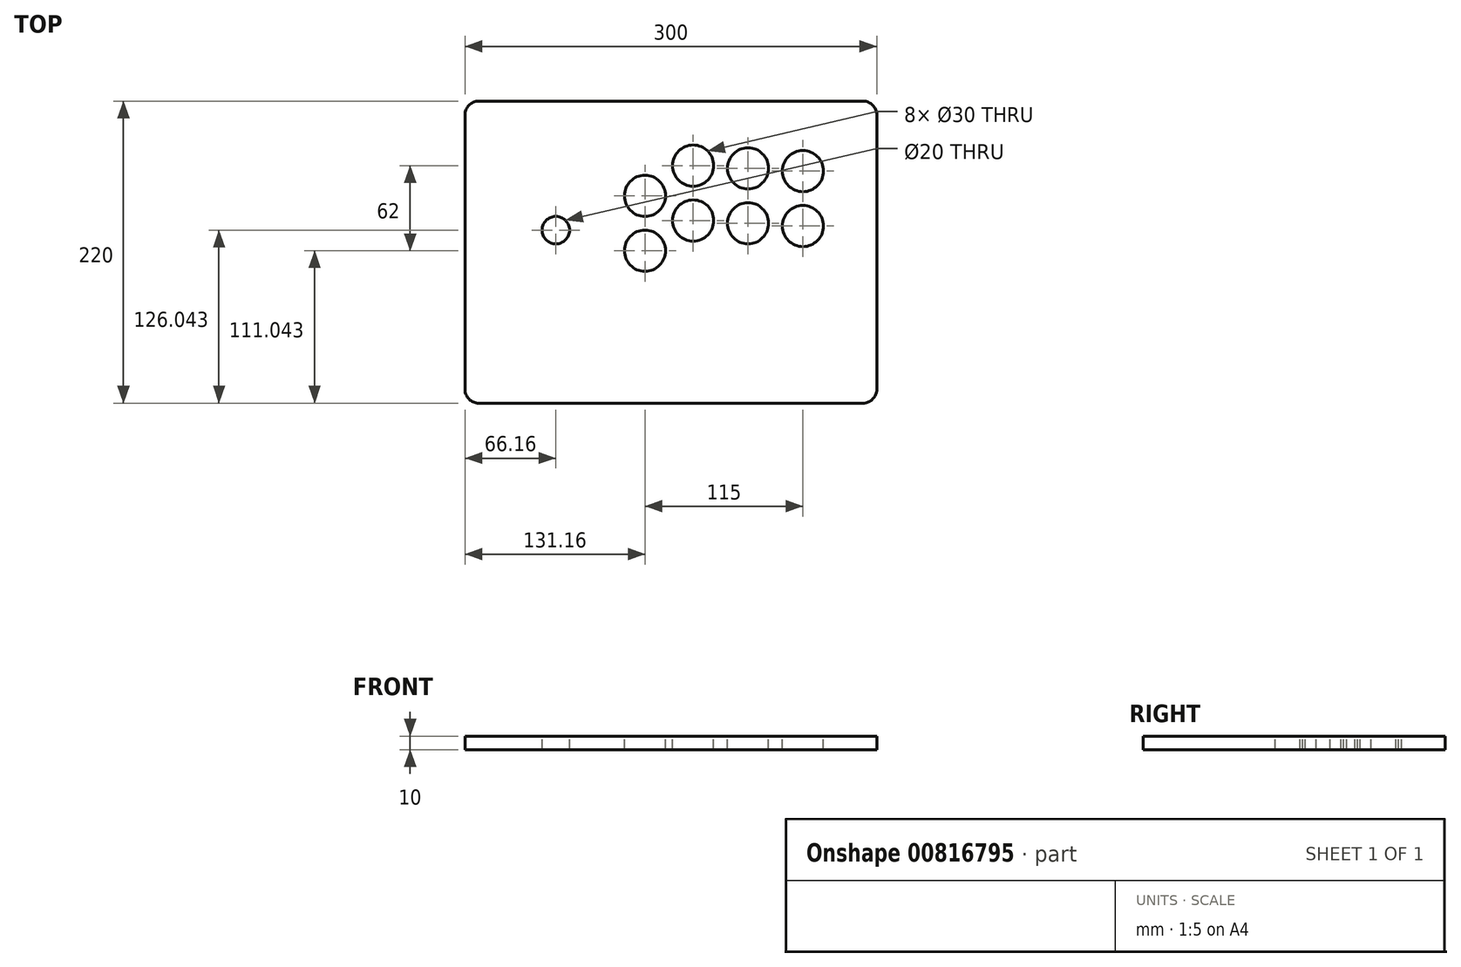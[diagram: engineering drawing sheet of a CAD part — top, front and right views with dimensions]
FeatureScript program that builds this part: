
annotation { "Feature Type Name" : "Feature", "Feature Type Description" : "" }
export const myFeature = defineFeature(function(context is Context, id is Id, definition is map)
    precondition{}
    {
        {
            var Q0;
            Q0=qCreatedBy(makeId("Top.planeOp"),FACE);
            var sketch = newSketch(context, id + "F0", { "sketchPlane" : qUnion([Q0])});
            skLineSegment(sketch, "E0.bottom", {"start": v(-140, 110) * mm, "end": v(140, 110) * mm});
            skLineSegment(sketch, "E0.top", {"start": v(-140, -110) * mm, "end": v(140, -110) * mm});
            skLineSegment(sketch, "E0.left", {"start": v(-150, 100) * mm, "end": v(-150, -100) * mm});
            skLineSegment(sketch, "E0.right", {"start": v(150, 100) * mm, "end": v(150, -100) * mm});
            skPoint(sketch, "E1.visualSharp", {"position": v(-150, 110) * mm});
            skArc(sketch, "E1.filletArc", {"start": v(-140, 110) * mm, "mid": v(-147.07, 107.07) * mm, "end": v(-150, 100) * mm});
            skArc(sketch, "E2.filletArc", {"start": v(-150, -100) * mm, "mid": v(-147.07, -107.07) * mm, "end": v(-140, -110) * mm});
            skArc(sketch, "E3.filletArc", {"start": v(140, -110) * mm, "mid": v(147.07, -107.07) * mm, "end": v(150, -100) * mm});
            skPoint(sketch, "E4.visualSharp", {"position": v(150, 110) * mm});
            skArc(sketch, "E4.filletArc", {"start": v(150, 100) * mm, "mid": v(147.07, 107.07) * mm, "end": v(140, 110) * mm});
            skSolve(sketch);
        }
        {
            var Q0;
            Q0=makeQuery(id+"F0.imprint","IMPRINT",FACE,{"disambiguationData":[TD([[makeQuery(id+"F0.imprint","IMPRINT",EDGE,{"derivedFrom":sQuery(id+"F0.wireOp",EDGE,"E0.bottom")}),-1.0]])]});
            extrude(context, id + "F1", {"entities" : qUnion([Q0]), "depth" : 10 * mm, "offsetDistance" : 25 * mm});
        }
        {
            var Q0;
            Q0=makeQuery(id+"F1.opExtrude","CAP_FACE",FACE,{"disambiguationData":[OSD([sQuery(id+"F0.wireOp",EDGE,"E0.bottom"),sQuery(id+"F0.wireOp",EDGE,"E0.top"),sQuery(id+"F0.wireOp",EDGE,"E0.left"),sQuery(id+"F0.wireOp",EDGE,"E0.right"),sQuery(id+"F0.wireOp",EDGE,"7U7vh1Hn-upP3-d99j-u4dh-bKfNenWRPj8P"),sQuery(id+"F0.wireOp",EDGE,"9KV0FTLN-cMhS-Cijb-6pHX-Euy8x6DlE4BF"),sQuery(id+"F0.wireOp",EDGE,"lCMdOSFM-ggo3-Ofda-7PvR-zEtVCtEVlDY4"),sQuery(id+"F0.wireOp",EDGE,"BKXtT0LE-fJT9-nw2k-YAUW-kZtXI7F3bTfB"),sQuery(id+"F0.wireOp",EDGE,"wV41daUc-EEE4-FCbd-12yS-wtypiBXCcxim"),sQuery(id+"F0.wireOp",EDGE,"khiqz8aN-VROC-6t9z-2kBw-9y2gaBjsAfUj"),sQuery(id+"F0.wireOp",EDGE,"t2eBG0hw-ZqrJ-Y5c7-V3vu-3pAyAulA7WG8"),sQuery(id+"F0.wireOp",EDGE,"ZSTTaZvo-njyQ-vZPK-0F9O-M3Yc0Q9PGQOn"),sQuery(id+"F0.wireOp",EDGE,"Gb1nHC3x-37tJ-bX3T-YIKq-VaC1Sf7oD8jA"),sQuery(id+"F0.wireOp",EDGE,"1LKZGN7T-XHOy-vLGE-QeC0-VbC3BGO08JDl"),sQuery(id+"F0.wireOp",EDGE,"22aeab33-8b55-4c08-b406-0674019cbc4c0.MirrorCS"),sQuery(id+"F0.wireOp",EDGE,"321f0d1a-5e38-4756-8316-7f71a36d44820.MirrorCS"),sQuery(id+"F0.wireOp",EDGE,"0364318f-eded-46c4-8251-821724c0179f0.MirrorCS"),sQuery(id+"F0.wireOp",EDGE,"9e6429c9-2306-4f91-a8b6-bbf118cb79580.MirrorCS"),sQuery(id+"F0.wireOp",EDGE,"2393fd1a-d5d7-4526-84b0-051bffbad2ec0.MirrorCS"),sQuery(id+"F0.wireOp",EDGE,"18ea4826-1af4-4759-ada8-3a0332edf3330.MirrorCS"),sQuery(id+"F0.wireOp",EDGE,"GNLDDBHi-NwgK-jo6X-WTo3-YKHwSXEjXMRN"),sQuery(id+"F0.wireOp",EDGE,"L9XWDe4h-B4Om-V65G-o8Nv-q2a5I2NxTQwa"),sQuery(id+"F0.wireOp",EDGE,"021xOwiZ-t5GJ-C9K5-q3xd-f7qZEb4f2LLx"),sQuery(id+"F0.wireOp",EDGE,"hp27QHDk-CRXm-L6vz-wJHl-bjtb0pbeazuK"),sQuery(id+"F0.wireOp",EDGE,"909844e4-ac14-440c-96fe-bf892719fdba0.MirrorCS"),sQuery(id+"F0.wireOp",EDGE,"515c4d56-e007-4bd4-92e1-d293d80807220.MirrorCS"),sQuery(id+"F0.wireOp",EDGE,"aa180e3c-d767-475b-a5de-03adfb5a723f0.MirrorCS"),sQuery(id+"F0.wireOp",EDGE,"7ca5c48a-416c-4eae-af14-6608fe3d942e0.MirrorCS"),sQuery(id+"F0.wireOp",EDGE,"9712f913-b60f-48b5-9bdd-8751214b1dcf0.MirrorCS"),sQuery(id+"F0.wireOp",EDGE,"9712f913-b60f-48b5-9bdd-8751214b1dcf1.MirrorCS"),sQuery(id+"F0.wireOp",EDGE,"9712f913-b60f-48b5-9bdd-8751214b1dcf2.MirrorCS"),sQuery(id+"F0.wireOp",EDGE,"9712f913-b60f-48b5-9bdd-8751214b1dcf3.MirrorCS"),sQuery(id+"F0.wireOp",EDGE,"9712f913-b60f-48b5-9bdd-8751214b1dcf4.MirrorCS"),sQuery(id+"F0.wireOp",EDGE,"9712f913-b60f-48b5-9bdd-8751214b1dcf5.MirrorCS"),sQuery(id+"F0.wireOp",EDGE,"9712f913-b60f-48b5-9bdd-8751214b1dcf6.MirrorCS"),sQuery(id+"F0.wireOp",EDGE,"9712f913-b60f-48b5-9bdd-8751214b1dcf7.MirrorCS"),sQuery(id+"F0.wireOp",EDGE,"9712f913-b60f-48b5-9bdd-8751214b1dcf8.MirrorCS"),sQuery(id+"F0.wireOp",EDGE,"9712f913-b60f-48b5-9bdd-8751214b1dcf9.MirrorCS"),sQuery(id+"F0.wireOp",EDGE,"9712f913-b60f-48b5-9bdd-8751214b1dcf10.MirrorCS"),sQuery(id+"F0.wireOp",EDGE,"9712f913-b60f-48b5-9bdd-8751214b1dcf11.MirrorCS"),sQuery(id+"F0.wireOp",EDGE,"9712f913-b60f-48b5-9bdd-8751214b1dcf12.MirrorCS"),sQuery(id+"F0.wireOp",EDGE,"9712f913-b60f-48b5-9bdd-8751214b1dcf13.MirrorCS"),sQuery(id+"F0.wireOp",EDGE,"9712f913-b60f-48b5-9bdd-8751214b1dcf14.MirrorCS"),sQuery(id+"F0.wireOp",EDGE,"9712f913-b60f-48b5-9bdd-8751214b1dcf15.MirrorCS"),sQuery(id+"F0.wireOp",EDGE,"9712f913-b60f-48b5-9bdd-8751214b1dcf16.MirrorCS"),sQuery(id+"F0.wireOp",EDGE,"9712f913-b60f-48b5-9bdd-8751214b1dcf17.MirrorCS"),sQuery(id+"F0.wireOp",EDGE,"9712f913-b60f-48b5-9bdd-8751214b1dcf18.MirrorCS"),sQuery(id+"F0.wireOp",EDGE,"9712f913-b60f-48b5-9bdd-8751214b1dcf19.MirrorCS"),sQuery(id+"F0.wireOp",EDGE,"66b4c140-4653-4547-9f45-8cdecd55a1b10.MirrorCS"),sQuery(id+"F0.wireOp",EDGE,"d3ddb692-ff40-49a0-bd96-d2e3a4bf780c0.MirrorCS"),sQuery(id+"F0.wireOp",EDGE,"dd6259fd-953e-4730-9673-8fbce7dc52270.MirrorCS"),sQuery(id+"F0.wireOp",EDGE,"642498de-7ea3-44bc-ab3e-f491a4e3645c0.MirrorCS"),sQuery(id+"F0.wireOp",EDGE,"f0062d4f-6e21-4852-82b3-49c725a454500.MirrorCS"),sQuery(id+"F0.wireOp",EDGE,"02249f16-d06e-4592-975d-b80ebbecdb0b0.MirrorCS"),sQuery(id+"F0.wireOp",EDGE,"6da44f19-4817-459e-ad64-d422597756450.MirrorCS"),sQuery(id+"F0.wireOp",EDGE,"c8a329ab-8926-40e7-a344-b33a86447da60.MirrorCS"),sQuery(id+"F0.wireOp",EDGE,"86bbf935-ceb7-4150-9a93-60763b190f840.MirrorCS"),sQuery(id+"F0.wireOp",EDGE,"97103ca1-3d53-498c-ac91-2f3e8dc6db9c0.MirrorCS"),sQuery(id+"F0.wireOp",EDGE,"1b8d340c-48f8-4480-ab45-95007611345c0.MirrorCS"),sQuery(id+"F0.wireOp",EDGE,"5dd018f6-8b73-4855-8f44-a4b58c8977af0.MirrorCS")])],"isStart":false});
            var sketch = newSketch(context, id + "F2", { "sketchPlane" : qUnion([Q0])});
            skLineSegment(sketch, "E5.bottom", {"start": v(-150, 110) * mm, "end": v(150, 110) * mm});
            skLineSegment(sketch, "E5.top", {"start": v(-150, -110) * mm, "end": v(150, -110) * mm});
            skLineSegment(sketch, "E5.left", {"start": v(-150, 110) * mm, "end": v(-150, -110) * mm});
            skLineSegment(sketch, "E5.right", {"start": v(150, 110) * mm, "end": v(150, -110) * mm});
            skPoint(sketch, "E5.middle", {"position": v(0, 0) * mm});
            skLineSegment(sketch, "E6", {"start": v(150, -110) * mm, "end": v(-69, -110) * mm});
            skCircle(sketch, "E7", {"center": v(96.16, 19.04) * mm, "radius": 15 * mm});
            skCircle(sketch, "E8", {"center": v(96.16, 59.04) * mm, "radius": 15 * mm});
            skCircle(sketch, "E9", {"center": v(56.16, 61.04) * mm, "radius": 15 * mm});
            skCircle(sketch, "E10", {"center": v(56.16, 21.04) * mm, "radius": 15 * mm});
            skCircle(sketch, "E11", {"center": v(16.16, 23.04) * mm, "radius": 15 * mm});
            skCircle(sketch, "E12", {"center": v(16.16, 63.04) * mm, "radius": 15 * mm});
            skCircle(sketch, "E13", {"center": v(-18.84, 1.04) * mm, "radius": 15 * mm});
            skCircle(sketch, "E14", {"center": v(-18.84, 41.04) * mm, "radius": 15 * mm});
            skCircle(sketch, "E15", {"center": v(-83.84, 16.04) * mm, "radius": 10 * mm});
            skSolve(sketch);
        }
        {
            var Q0;
            Q0=makeQuery(id+"F2.imprint","IMPRINT",FACE,{"disambiguationData":[TD([[makeQuery(id+"F2.imprint","IMPRINT",EDGE,{"derivedFrom":sQuery(id+"F2.wireOp",EDGE,"E15")}),1.0]])]});
            var Q1;
            Q1=makeQuery(id+"F2.imprint","IMPRINT",FACE,{"disambiguationData":[TD([[makeQuery(id+"F2.imprint","IMPRINT",EDGE,{"derivedFrom":sQuery(id+"F2.wireOp",EDGE,"E14")}),1.0]])]});
            var Q2;
            Q2=makeQuery(id+"F2.imprint","IMPRINT",FACE,{"disambiguationData":[TD([[makeQuery(id+"F2.imprint","IMPRINT",EDGE,{"derivedFrom":sQuery(id+"F2.wireOp",EDGE,"E12")}),1.0]])]});
            var Q3;
            Q3=makeQuery(id+"F2.imprint","IMPRINT",FACE,{"disambiguationData":[TD([[makeQuery(id+"F2.imprint","IMPRINT",EDGE,{"derivedFrom":sQuery(id+"F2.wireOp",EDGE,"E9")}),1.0]])]});
            var Q4;
            Q4=makeQuery(id+"F2.imprint","IMPRINT",FACE,{"disambiguationData":[TD([[makeQuery(id+"F2.imprint","IMPRINT",EDGE,{"derivedFrom":sQuery(id+"F2.wireOp",EDGE,"E8")}),1.0]])]});
            var Q5;
            Q5=makeQuery(id+"F2.imprint","IMPRINT",FACE,{"disambiguationData":[TD([[makeQuery(id+"F2.imprint","IMPRINT",EDGE,{"derivedFrom":sQuery(id+"F2.wireOp",EDGE,"E7")}),1.0]])]});
            var Q6;
            Q6=makeQuery(id+"F2.imprint","IMPRINT",FACE,{"disambiguationData":[TD([[makeQuery(id+"F2.imprint","IMPRINT",EDGE,{"derivedFrom":sQuery(id+"F2.wireOp",EDGE,"E10")}),1.0]])]});
            var Q7;
            Q7=makeQuery(id+"F2.imprint","IMPRINT",FACE,{"disambiguationData":[TD([[makeQuery(id+"F2.imprint","IMPRINT",EDGE,{"derivedFrom":sQuery(id+"F2.wireOp",EDGE,"E11")}),1.0]])]});
            var Q8;
            Q8=makeQuery(id+"F2.imprint","IMPRINT",FACE,{"disambiguationData":[TD([[makeQuery(id+"F2.imprint","IMPRINT",EDGE,{"derivedFrom":sQuery(id+"F2.wireOp",EDGE,"E13")}),1.0]])]});
            extrude(context, id + "F3", {"entities" : qUnion([Q0, Q1, Q2, Q3, Q4, Q5, Q6, Q7, Q8]), "operationType" : NewBodyOperationType.REMOVE, "oppositeDirection" : true, "depth" : 10 * mm, "offsetDistance" : 25 * mm});
        }
    });
